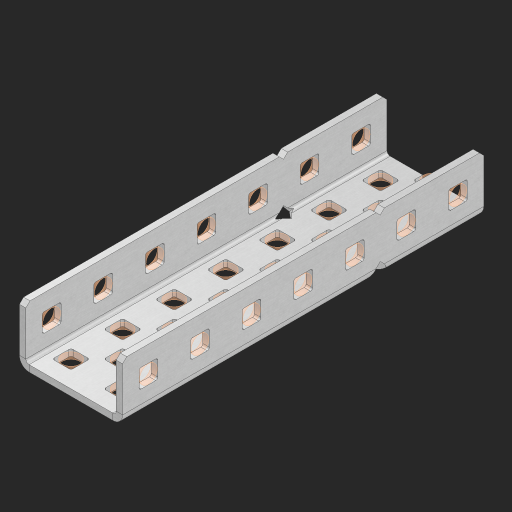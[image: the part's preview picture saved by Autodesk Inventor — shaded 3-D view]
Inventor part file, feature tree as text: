
AUTODESK INVENTOR PART (.ipt)
format: ipt  version: 2023 (Build 270158000, 158)  size: 811,008 bytes
history: native  units: in
note: dims shown in document units (in); Inventor stores cm internally (conversion verified against a paired STEP export)
features: other x42, extrude x33, sheet_metal_op x11, sketch x10, pattern_linear x2, mirror x1, chamfer x1
ambient origin geometry x8: Origin, YZ Plane, XZ Plane, XY Plane, X Axis, Y Axis, Z Axis, Center Point
bodies: Solid1 (feature_tree), Body (feature_tree)
feature tree (100):
  sheet_metal_op  "Flanges"
  other  "Flange Pattern Plane"
  other  "Flange Pattern Sketch"
  sheet_metal_op  "Flange Pattern"
  sheet_metal_op  "Body Pattern"
  pattern_linear  "Center Pattern"  Spacing1=0.0625in  [1 undecoded]
  other  "Arc Length"
  mirror  "Notch Mirror"
  pattern_linear  "Notch Pattern"  Spacing1=0.182in  [1 undecoded]
  chamfer  "End Chamfer"
  extrude  "Half Cut"  Depth=0.02in
  sketch  "Sketch1"  dims[d0=1.0in]
  other  "Plate1"
  sketch  "Sketch2"  dims[d1=3.5in]
  other  "Plate2"
  sheet_metal_op  "Bend1"
  sheet_metal_op  "Corner1"
  sketch  "Sketch3"  dims[d2=0.0625in]
  sketch  "Sketch7"  dims[d3=0.0625in]
  other  "Srf1"
  other  "Srf2"
  sketch  "Sketch8"  dims[d4=0.0312in]
  sketch  "Sketch9"  dims[d5=0.125in]
  other  "Srf91"
  sheet_metal_op  "Body Pattern Sketch"
  other  "Srf92"
  sketch  "Sketch13"  dims[d6=0.0625in]
  sketch  "Sketch14"  dims[d7=0.5in d8=90.0deg d9=0.0312in]
  sketch  "Sketch15"  dims[d10=0.25in]
  sketch  "Sketch16"  dims[d11=0.0625in d12=0.0625in d16=0.182in d17=0.02in d18=0.0625in d19=0.0in d20=0.25in d21=0.25in d38=2.7559in d40=0.5in d41=0.7874in d43=1.0in d46=0.172in d47=1.0in d48=0.0in d49=0.182in d50=0.02in d51=0.25in d52=0.25in d53=0.0625in d54=0.0in d55=0.172in d56=1.0in d57=0.0in d58=0.25in d60=2.7559in d62=0.5in d63=0.7874in d65=0.5in d85=0.1473in d86=0.1782in d88=0.04in d89=0.0625in d90=0.0in d91=0.04in d92=0.0491in d95=2.5in d96=0.04in d97=0.25in d98=45.0deg d99=0.25in d100=0.5in d101=0.0in d102=2.497in d106=0.182in d107=0.02in d108=0.5in d109=0.5in d110=0.0625in d111=0.0in d112=0.172in d113=0.5in d114=0.0in d117=0.5in d118=0.5in d119=0.5in]
  other  "Srf786"
  other  "Srf823"
  other  "Srf824"
  other  "Srf825"
  other  "Srf826"
  other  "Srf827"
  other  "Srf828"
  other  "Srf829"
  other  "Srf856"
  other  "Srf857"
  other  "Srf858"
  other  "Srf859"
  other  "Srf860"
  other  "Srf861"
  other  "Srf862"
  other  "Srf889"
  other  "Srf890"
  other  "Srf891"
  other  "Srf892"
  other  "Srf893"
  other  "Srf894"
  other  "Srf922"
  other  "Srf923"
  other  "Srf924"
  other  "Srf925"
  other  "Srf926"
  other  "Srf959"
  other  "Srf960"
  other  "Srf961"
  other  "Srf962"
  other  "Srf963"
  sheet_metal_op  "Flange Stamp"
  sheet_metal_op  "Flange Circle"
  sheet_metal_op  "Body Stamp"
  sheet_metal_op  "Body Circle"
  other  "Center Stamp"
  other  "Center Circle"
  sheet_metal_op  "Notch"
  extrude  "ExtrusionSrf2"  Depth=0.0625in
  extrude  "ExtrusionSrf92"  TaperAngle=0.0deg  [1 undecoded]
  extrude  "ExtrusionSrf823"  Depth=0.5in
  extrude  "ExtrusionSrf824"  Depth=0.5in
  extrude  "ExtrusionSrf825"  Depth=0.5in
  extrude  "ExtrusionSrf826"  Depth=0.5in
  extrude  "ExtrusionSrf827"  Depth=1.0in TaperAngle=0.0deg
  extrude  "ExtrusionSrf828"  Depth=0.5in
  extrude  "ExtrusionSrf829"  Depth=0.02in
  extrude  "ExtrusionSrf856"  Depth=0.5in
  extrude  "ExtrusionSrf857"  Depth=0.5in
  extrude  "ExtrusionSrf858"  Depth=0.0625in
  extrude  "ExtrusionSrf859"  TaperAngle=0.0deg  [1 undecoded]
  extrude  "ExtrusionSrf860"  Depth=0.5in
  extrude  "ExtrusionSrf861"  Depth=1.0in TaperAngle=0.0deg
  extrude  "ExtrusionSrf862"  Depth=0.5in
  extrude  "ExtrusionSrf889"  Depth=0.5in
  extrude  "ExtrusionSrf890"  Depth=0.5in
  extrude  "ExtrusionSrf891"  Depth=0.5in
  extrude  "ExtrusionSrf892"  Depth=0.5in
  extrude  "ExtrusionSrf893"  Depth=0.5in
  extrude  "ExtrusionSrf894"  Depth=0.0625in
  extrude  "ExtrusionSrf922"  TaperAngle=0.0deg  [1 undecoded]
  extrude  "ExtrusionSrf923"  Depth=0.5in
  extrude  "ExtrusionSrf924"  Depth=0.5in
  extrude  "ExtrusionSrf925"  Depth=2.5in
  extrude  "ExtrusionSrf926"  Depth=0.5in TaperAngle=45.0deg
  extrude  "ExtrusionSrf959"  Depth=0.5in
  extrude  "ExtrusionSrf960"  Depth=0.5in TaperAngle=0.0deg
  extrude  "ExtrusionSrf961"  Depth=0.5in
  extrude  "ExtrusionSrf962"  Depth=0.5in
  extrude  "ExtrusionSrf963"  Depth=0.02in
note: 5 required parameter values undecoded (feature->parameter linkage not recoverable at this tier; creation-order binding heuristic only, values carry confidence <= 0.55)
